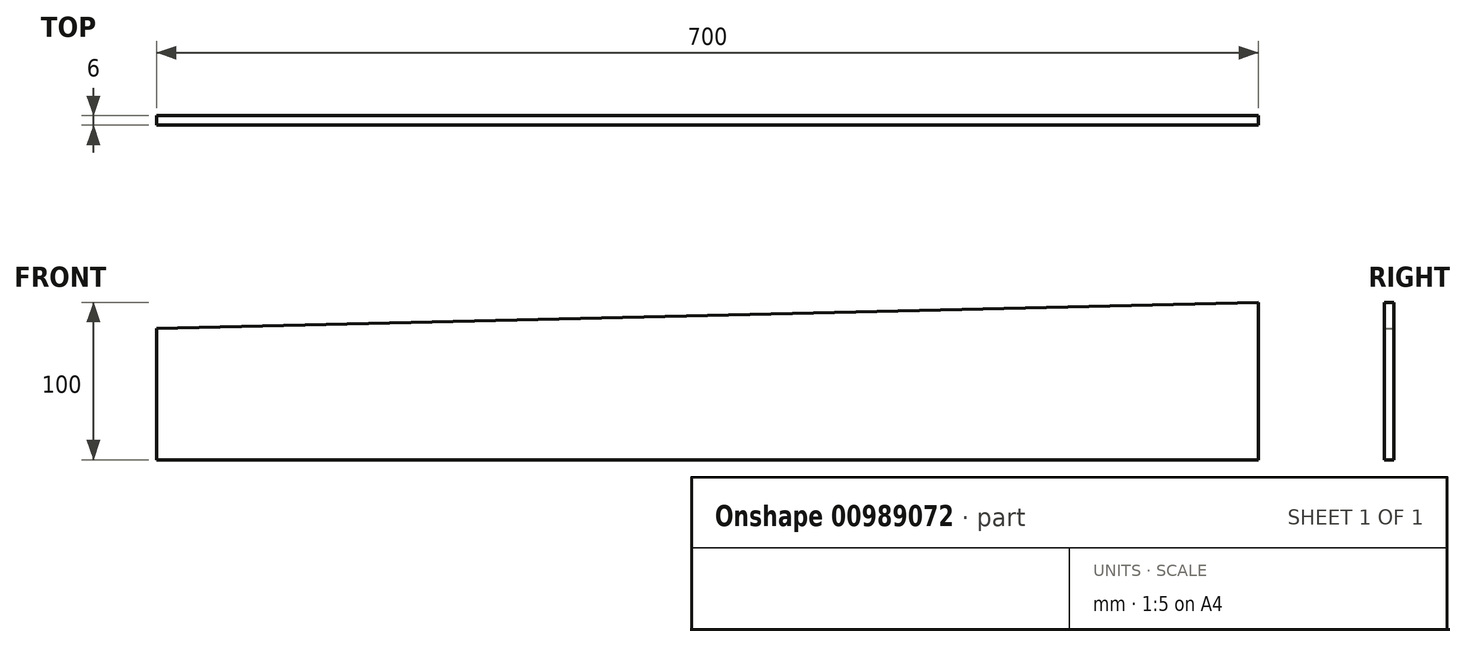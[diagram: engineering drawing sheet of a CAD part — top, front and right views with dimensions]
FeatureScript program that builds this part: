
annotation { "Feature Type Name" : "Feature", "Feature Type Description" : "" }
export const myFeature = defineFeature(function(context is Context, id is Id, definition is map)
    precondition{}
    {
        {
            var Q0;
            Q0=qCreatedBy(makeId("Front.planeOp"),FACE);
            var sketch = newSketch(context, id + "F0", { "sketchPlane" : qUnion([Q0])});
            skLineSegment(sketch, "E0", {"start": v(1050, -37.5) * mm, "end": v(1050, 62.5) * mm});
            skLineSegment(sketch, "E1", {"start": v(1050, -37.5) * mm, "end": v(-1050, -37.5) * mm});
            skLineSegment(sketch, "E2", {"start": v(-1050, -37.5) * mm, "end": v(-1050, 12.5) * mm});
            skLineSegment(sketch, "E3", {"start": v(-1050, 12.5) * mm, "end": v(1050, 62.5) * mm});
            skLineSegment(sketch, "E4", {"start": v(-350, -37.5) * mm, "end": v(-350, 29.17) * mm});
            skLineSegment(sketch, "E5", {"start": v(350, -37.5) * mm, "end": v(350, 45.83) * mm});
            skSolve(sketch);
        }
        {
            var Q0;
            Q0=makeQuery(id+"F0.imprint","IMPRINT",FACE,{"disambiguationData":[TD([[makeQuery(id+"F0.imprint","IMPRINT",EDGE,{"derivedFrom":sQuery(id+"F0.wireOp",EDGE,"E0")}),1.0]])]});
            extrude(context, id + "F1", {"entities" : qUnion([Q0]), "depth" : 6 * mm, "offsetDistance" : 25 * mm});
        }
    });
